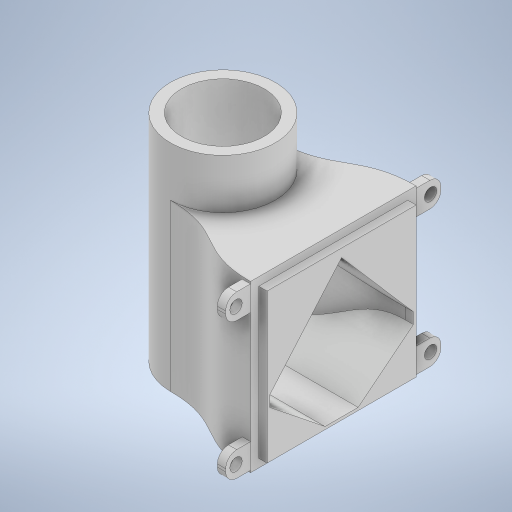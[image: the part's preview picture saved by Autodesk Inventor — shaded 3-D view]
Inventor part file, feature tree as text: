
AUTODESK INVENTOR PART (.ipt)
format: ipt  version: 2024 (Build 280153000, 153)  size: 458,240 bytes
history: native  units: in
note: dims shown in document units (in); Inventor stores cm internally (conversion verified against a paired STEP export)
features: extrude x7, sketch x6, projected_geometry x2, plane x1, hole x1, fillet x1
ambient origin geometry x8: Origin, YZ Plane, XZ Plane, XY Plane, X Axis, Y Axis, Z Axis, Center Point
bodies: Solid1 (feature_tree)
feature tree (18):
  extrude  "Extrusion1"  Depth=0.0787in
  plane  "Work Plane1"
  extrude  "Extrusion2"  Depth=0.374in
  sketch  "Sketch4"  dims[d5=1.1811in d6=0.0787in]
  extrude  "Extrusion4"  Depth=0.0787in
  hole  "Hole2"  [1 undecoded]
  sketch  "Sketch9"  dims[d10=0.5118in d11=0.1181in]
  extrude  "Extrusion7"  Depth=0.1181in
  extrude  "Extrusion8"  Depth=0.1772in
  extrude  "Extrusion9"  Depth=0.0787in
  extrude  "Extrusion3"  Depth=0.0787in
  fillet  "Fillet1"  Radius=0.0787in
  sketch  "Sketch1"  dims[d0=0.748in d1=0.0787in]
  sketch  "Sketch2"  dims[d2=0.4724in d3=0.0in d4=0.374in]
  projected_geometry  "Projected Loop1"
  sketch  "Sketch8"  dims[d7=0.0787in d9=1.0236in]
  projected_geometry  "Projected Loop5"
  sketch  "Sketch11"  dims[d12=0.1181in d13=1.1811in d16=0.4724in d17=0.0787in d18=0.0787in d20=0.0787in d21=0.2362in d22=0.1181in d23=0.4724in d24=0.0in d25=0.0886in d26=1.1811in d27=1.1811in d35=0.0591in d36=0.2362in d37=0.0in d38=0.0591in d39=0.0in d40=0.748in d41=0.0in d53=0.5906in d54=0.1033in d55=0.1033in d56=0.1033in d57=0.1033in d58=0.1033in d60=0.1033in d61=0.1033in d62=0.5906in d63=0.2362in d64=0.1575in d65=0.0787in d66=90.0deg d67=0.3937in d68=0.8108in d69=0.7874in d70=0.0787in d71=0.0787in d72=0.0in d73=0.0in d74=1.1811in d75=0.0in d76=0.1033in d77=0.1033in d78=0.1033in d79=0.1033in d80=0.1772in d82=0.1772in d86=0.0591in d87=0.0in d91=0.0787in d92=0.0148in d93=0.0886in d94=0.1772in d95=0.1772in d96=0.0148in d97=0.315in d98=0.315in]
note: 1 required parameter value undecoded (feature->parameter linkage not recoverable at this tier; creation-order binding heuristic only, values carry confidence <= 0.55)
